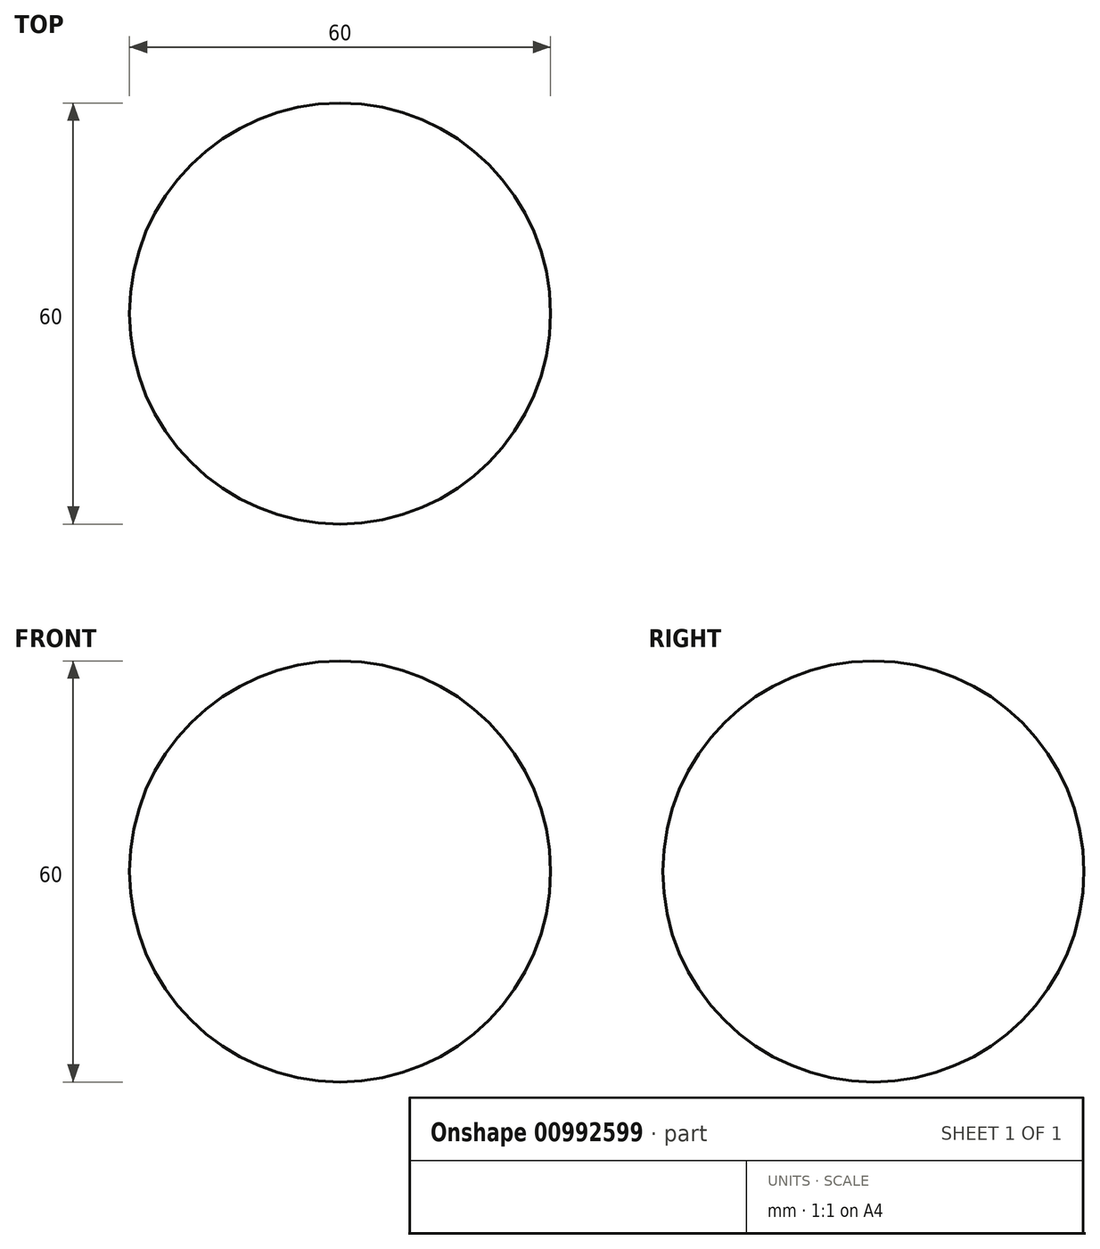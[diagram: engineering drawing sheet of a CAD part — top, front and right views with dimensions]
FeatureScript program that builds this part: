
annotation { "Feature Type Name" : "Feature", "Feature Type Description" : "" }
export const myFeature = defineFeature(function(context is Context, id is Id, definition is map)
    precondition{}
    {
        {
            var Q0;
            Q0=qCreatedBy(makeId("Front.planeOp"),FACE);
            var sketch = newSketch(context, id + "F0", { "sketchPlane" : qUnion([Q0])});
            skArc(sketch, "E0", {"start": v(0, -30) * mm, "mid": v(30, 0) * mm, "end": v(0, 30) * mm});
            skLineSegment(sketch, "E1", {"start": v(0, 30) * mm, "end": v(0, -30) * mm});
            skSolve(sketch);
        }
        {
            var Q0;
            Q0=makeQuery(id+"F0.imprint","IMPRINT",FACE,{"disambiguationData":[TD([[makeQuery(id+"F0.imprint","IMPRINT",EDGE,{"derivedFrom":sQuery(id+"F0.wireOp",EDGE,"E0")}),1.0]])]});
            var Q1;
            Q1=sQuery(id+"F0.wireOp",EDGE,"E1");
            revolve(context, id + "F1", {"surfaceOperationType" : NewSurfaceOperationType.NEW, "entities" : qUnion([Q0]), "axis" : qUnion([Q1]), "revolveType" : RevolveType.FULL});
        }
    });
